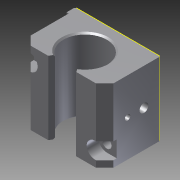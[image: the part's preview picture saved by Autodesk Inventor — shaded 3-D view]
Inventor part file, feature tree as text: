
AUTODESK INVENTOR PART (.ipt)
format: ipt  version: 2013 (Build 170138000, 138)  size: 144,384 bytes
history: native  units: in
note: dims shown in document units (in); Inventor stores cm internally (conversion verified against a paired STEP export)
features: sketch x1, imported_body x1
ambient origin geometry x8: Origin, YZ Plane, XZ Plane, XY Plane, X Axis, Y Axis, Z Axis, Center Point
feature tree (2):
  sketch  "Sketch1"  dims[d0=0.5315in d1=0.315in]
  imported_body  "Base1"
